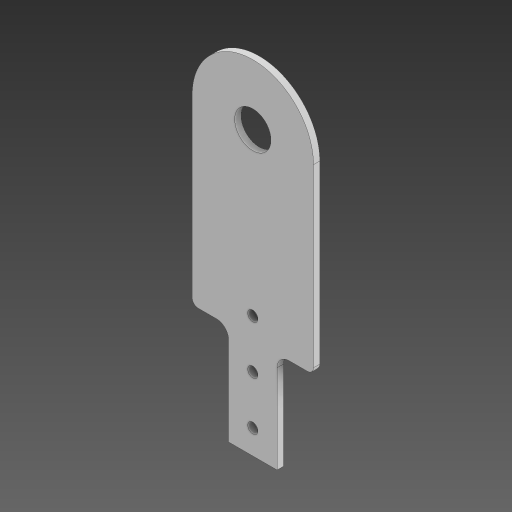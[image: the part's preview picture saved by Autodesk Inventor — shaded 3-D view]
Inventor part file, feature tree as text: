
AUTODESK INVENTOR PART (.ipt)
format: ipt  version: 2024 (Build 280153000, 153)  size: 213,504 bytes
history: native  units: in
note: dims shown in document units (in); Inventor stores cm internally (conversion verified against a paired STEP export)
features: fillet x5, other x1, extrude x1, sketch x1
ambient origin geometry x8: Origin, YZ Plane, XZ Plane, XY Plane, X Axis, Y Axis, Z Axis, Center Point
bodies: Solid1 (feature_tree)
feature tree (8):
  other  "Wrist plate"
  extrude  "Extrusion1"  Depth=5.0in
  fillet  "Fillet1"  Radius=0.748in
  fillet  "Fillet2"  Radius=0.209in
  fillet  "Fillet3"  Radius=0.209in
  fillet  "Fillet4"  Radius=1.25in
  fillet  "Fillet5"  Radius=4.575in
  sketch  "Sketch1"  dims[d0=2.5in d1=5.0in d2=0.748in d3=0.209in d4=0.209in d5=1.25in d6=4.575in d8=0.13in d9=0.0in d10=1.25in d11=1.25in d12=0.125in d13=0.125in d14=1.0in d15=1.0in d17=1.0in d18=0.25in d20=1.5573in d21=0.5in]
